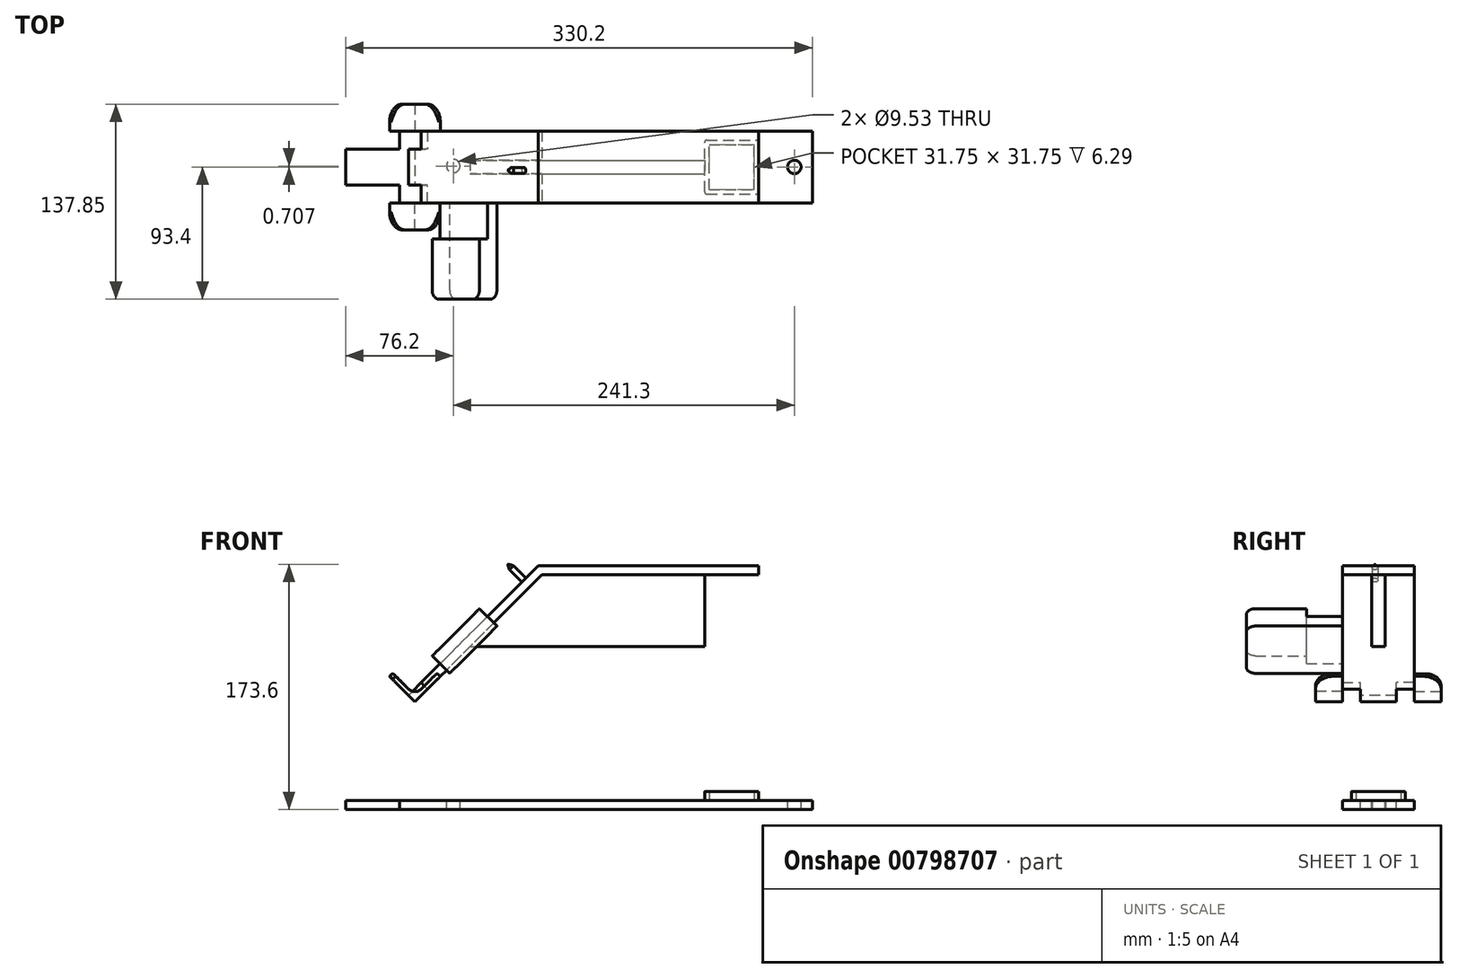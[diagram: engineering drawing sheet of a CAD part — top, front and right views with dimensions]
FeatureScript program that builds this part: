
annotation { "Feature Type Name" : "Feature", "Feature Type Description" : "" }
export const myFeature = defineFeature(function(context is Context, id is Id, definition is map)
    precondition{}
    {
        {
            assignVariable(context, id + "F0", {"name" : "haut", "anyValue" : 8 - 0.49 - 1 - .25 + 0.03});
        }
        {
            var Q0;
            Q0=qCreatedBy(makeId("Top.planeOp"),FACE);
            var sketch = newSketch(context, id + "F1", { "sketchPlane" : qUnion([Q0])});
            skLineSegment(sketch, "E0.bottom", {"start": v(0, 0) * mm, "end": v(114.3, 0) * mm});
            skLineSegment(sketch, "E0.top", {"start": v(0, 50.8) * mm, "end": v(114.3, 50.8) * mm});
            skLineSegment(sketch, "E0.left", {"start": v(0, 0) * mm, "end": v(0, 50.8) * mm});
            skLineSegment(sketch, "E0.right", {"start": v(114.3, 0) * mm, "end": v(114.3, 50.8) * mm});
            skLineSegment(sketch, "E1.bottom", {"start": v(0, 0) * mm, "end": v(-177.8, 0) * mm});
            skLineSegment(sketch, "E1.top", {"start": v(0, 50.8) * mm, "end": v(-177.8, 50.8) * mm});
            skLineSegment(sketch, "E1.right", {"start": v(-215.9, 12.7) * mm, "end": v(-215.9, 38.1) * mm});
            skLineSegment(sketch, "E2.top", {"start": v(-215.9, 38.1) * mm, "end": v(-177.8, 38.1) * mm});
            skLineSegment(sketch, "E2.right", {"start": v(-177.8, 50.8) * mm, "end": v(-177.8, 38.1) * mm});
            skLineSegment(sketch, "E3.top", {"start": v(-215.9, 12.7) * mm, "end": v(-177.8, 12.7) * mm});
            skLineSegment(sketch, "E3.right", {"start": v(-177.8, 0) * mm, "end": v(-177.8, 12.7) * mm});
            skCircle(sketch, "E4", {"center": v(101.6, 25.4) * mm, "radius": 4.76 * mm});
            skCircle(sketch, "E5", {"center": v(-139.7, 26.1) * mm, "radius": 4.76 * mm});
            skSolve(sketch);
        }
        {
            var Q0;
            Q0=qSketchRegion(id+"F1",true);
            extrude(context, id + "F2", {"entities" : qUnion([Q0]), "oppositeDirection" : true, "depth" : 6.35 * mm, "offsetDistance" : 25.4 * mm});
        }
        {
            var Q0;
            Q0=makeQuery(id+"F2.opExtrude","CAP_FACE",FACE,{"disambiguationData":[OSD([sQuery(id+"F1.wireOp",EDGE,"E0.bottom"),sQuery(id+"F1.wireOp",EDGE,"E0.top"),sQuery(id+"F1.wireOp",EDGE,"E0.left"),sQuery(id+"F1.wireOp",EDGE,"E0.right")])],"isStart":true});
            var sketch = newSketch(context, id + "F3", { "sketchPlane" : qUnion([Q0])});
            skLineSegment(sketch, "E6.bottom", {"start": v(38.1, 6.35) * mm, "end": v(76.2, 6.35) * mm});
            skLineSegment(sketch, "E6.top", {"start": v(38.1, 44.45) * mm, "end": v(76.2, 44.45) * mm});
            skLineSegment(sketch, "E6.left", {"start": v(38.1, 6.35) * mm, "end": v(38.1, 44.45) * mm});
            skLineSegment(sketch, "E6.right", {"start": v(76.2, 6.35) * mm, "end": v(76.2, 44.45) * mm});
            skLineSegment(sketch, "E7.0", {"start": v(41.27, 41.28) * mm, "end": v(73.03, 41.28) * mm});
            skLineSegment(sketch, "E7.1", {"start": v(41.27, 9.52) * mm, "end": v(41.27, 41.28) * mm});
            skLineSegment(sketch, "E7.2", {"start": v(41.27, 9.52) * mm, "end": v(73.03, 9.53) * mm});
            skLineSegment(sketch, "E7.3", {"start": v(73.03, 9.53) * mm, "end": v(73.03, 41.28) * mm});
            skSolve(sketch);
        }
        {
            var Q0;
            Q0=qSketchRegion(id+"F3",true);
            extrude(context, id + "F4", {"entities" : qUnion([Q0]), "operationType" : NewBodyOperationType.ADD, "depth" : (getVariable(context, 'haut')) * mm, "offsetDistance" : 25.4 * mm});
        }
        {
            var Q0;
            Q0=makeQuery(id+"F4.opExtrude","SWEPT_FACE",FACE,{"disambiguationData":[OSD([sQuery(id+"F3.wireOp",EDGE,"E6.bottom")])]});
            var sketch = newSketch(context, id + "F5", { "sketchPlane" : qUnion([Q0])});
            skLineSegment(sketch, "E8", {"start": v(76.2, 159.77) * mm, "end": v(-77.04, 159.77) * mm});
            skLineSegment(sketch, "E9", {"start": v(-77.04, 159.77) * mm, "end": v(-166.85, 69.96) * mm});
            skLineSegment(sketch, "E10.0", {"start": v(76.2, 166.12) * mm, "end": v(-79.67, 166.12) * mm});
            skLineSegment(sketch, "E11.0", {"start": v(-79.67, 166.12) * mm, "end": v(-171.34, 74.45) * mm});
            skLineSegment(sketch, "E12", {"start": v(-166.85, 69.96) * mm, "end": v(-171.34, 74.45) * mm});
            skLineSegment(sketch, "E13", {"start": v(76.2, 159.77) * mm, "end": v(76.2, 166.12) * mm});
            skSolve(sketch);
        }
        {
            var Q0;
            Q0=qSketchRegion(id+"F5",true);
            extrude(context, id + "F6", {"entities" : qUnion([Q0]), "operationType" : NewBodyOperationType.ADD, "oppositeDirection" : true, "depth" : 44.45 * mm, "offsetDistance" : 25.4 * mm, "hasSecondDirection" : true, "secondDirectionOppositeDirection" : false, "secondDirectionDepth" : 6.35 * mm});
        }
        {
            var Q0;
            Q0=makeQuery(id+"F6.opExtrude","SWEPT_FACE",FACE,{"disambiguationData":[OSD([sQuery(id+"F5.wireOp",EDGE,"E11.0")])]});
            var sketch = newSketch(context, id + "F7", { "sketchPlane" : qUnion([Q0])});
            skCircle(sketch, "E14", {"center": v(-23.02, 46.84) * mm, "radius": 2.04 * mm});
            skLineSegment(sketch, "E15.direction1", {"start": v(-23.02, 46.84) * mm, "end": v(2.38, 46.84) * mm, "construction": true});
            skLineSegment(sketch, "E15.direction2", {"start": v(-23.02, 46.84) * mm, "end": v(-23.02, -80.16) * mm, "construction": true});
            skSolve(sketch);
        }
        {
            var Q0;
            Q0=qSketchRegion(id+"F7",true);
            extrude(context, id + "F8", {"entities" : qUnion([Q0]), "operationType" : NewBodyOperationType.ADD, "depth" : 15.88 * mm, "offsetDistance" : 25.4 * mm});
        }
        {
            var Q0;
            Q0=makeQuery(id+"F8.opExtrude","CAP_EDGE",EDGE,{"disambiguationData":[OSD([sQuery(id+"F7.wireOp",EDGE,"E14")])],"isStart":false});
            var Q1;
            Q1=makeQuery(id+"F8.opExtrude","CAP_EDGE",EDGE,{"disambiguationData":[OSD([sQuery(id+"F7.wireOp",EDGE,"E15.0.1.0")])],"isStart":false});
            chamfer(context, id + "F9", {"entities" : qUnion([Q0, Q1]), "chamferType" : ChamferType.OFFSET_ANGLE, "width" : 2.03 * mm, "oppositeDirection" : false, "angle" : 60 * degree, "tangentPropagation" : true});
        }
        {
            var Q0;
            Q0=makeQuery(id+"F7.imprint","IMPRINT",FACE,{"disambiguationData":[TD([[makeQuery(id+"F7.imprint","IMPRINT",EDGE,{"derivedFrom":sQuery(id+"F7.wireOp",EDGE,"E14")}),-1.0]])]});
            var sketch = newSketch(context, id + "F10", { "sketchPlane" : qUnion([Q0])});
            skLineSegment(sketch, "E16.bottom", {"start": v(-50.8, -68.5) * mm, "end": v(-38.1, -68.5) * mm});
            skLineSegment(sketch, "E16.top", {"start": v(-50.8, -55.8) * mm, "end": v(-38.1, -55.8) * mm});
            skLineSegment(sketch, "E16.left", {"start": v(-50.8, -68.5) * mm, "end": v(-50.8, -55.8) * mm});
            skLineSegment(sketch, "E16.right", {"start": v(-38.1, -68.5) * mm, "end": v(-38.1, -55.8) * mm});
            skLineSegment(sketch, "E17.bottom", {"start": v(0, -68.5) * mm, "end": v(-12.7, -68.5) * mm});
            skLineSegment(sketch, "E17.top", {"start": v(0, -55.8) * mm, "end": v(-12.7, -55.8) * mm});
            skLineSegment(sketch, "E17.left", {"start": v(0, -68.5) * mm, "end": v(0, -55.8) * mm});
            skLineSegment(sketch, "E17.right", {"start": v(-12.7, -68.5) * mm, "end": v(-12.7, -55.8) * mm});
            skSolve(sketch);
        }
        {
            var Q0;
            Q0=qSketchRegion(id+"F10",true);
            extrude(context, id + "F11", {"entities" : qUnion([Q0]), "operationType" : NewBodyOperationType.REMOVE, "oppositeDirection" : true, "depth" : 25.4 * mm, "offsetDistance" : 25.4 * mm});
        }
        {
            var Q0;
            Q0=makeQuery(id+"F6.opExtrude","CAP_FACE",FACE,{"disambiguationData":[OSD([sQuery(id+"F5.wireOp",EDGE,"E8"),sQuery(id+"F5.wireOp",EDGE,"E9"),sQuery(id+"F5.wireOp",EDGE,"E10.0"),sQuery(id+"F5.wireOp",EDGE,"E11.0"),sQuery(id+"F5.wireOp",EDGE,"E12"),sQuery(id+"F5.wireOp",EDGE,"E13")])],"isStart":false});
            var sketch = newSketch(context, id + "F12", { "sketchPlane" : qUnion([Q0])});
            skLineSegment(sketch, "E18", {"start": v(148.89, 87.92) * mm, "end": v(166.85, 69.96) * mm});
            skLineSegment(sketch, "E19", {"start": v(148.89, 87.92) * mm, "end": v(151.13, 90.17) * mm});
            skLineSegment(sketch, "E20", {"start": v(166.85, 69.96) * mm, "end": v(184.8, 87.92) * mm});
            skLineSegment(sketch, "E21.0", {"start": v(151.13, 90.17) * mm, "end": v(166.85, 74.45) * mm});
            skLineSegment(sketch, "E22.0", {"start": v(166.85, 74.45) * mm, "end": v(182.56, 90.17) * mm});
            skLineSegment(sketch, "E23.0", {"start": v(182.56, 90.17) * mm, "end": v(184.8, 87.92) * mm});
            skSolve(sketch);
        }
        {
            var Q0;
            Q0=qSketchRegion(id+"F12",true);
            extrude(context, id + "F13", {"entities" : qUnion([Q0]), "depth" : 19.05 * mm, "offsetDistance" : 25.4 * mm});
        }
        {
            var Q0;
            Q0=makeQuery(id+"F13.opExtrude","CAP_EDGE",EDGE,{"disambiguationData":[OSD([sQuery(id+"F12.wireOp",EDGE,"E23.0")])],"isStart":false});
            fillet(context, id + "F14", {"entities" : qUnion([Q0]), "radius" : 12.7 * mm, "tangentPropagation" : true, "allowEdgeOverflow" : false});
        }
        {
            var Q0;
            Q0=makeQuery(id+"F13.opExtrude","CAP_EDGE",EDGE,{"disambiguationData":[OSD([sQuery(id+"F12.wireOp",EDGE,"E19")])],"isStart":false});
            fillet(context, id + "F15", {"entities" : qUnion([Q0]), "radius" : 12.7 * mm, "tangentPropagation" : true, "allowEdgeOverflow" : false});
        }
        {
            var Q0;
            Q0=makeQuery(id+"F13.opExtrude","SWEPT_EDGE",EDGE,{"disambiguationData":[OSD([sQuery(id+"F12.wireOp",EDGE,"E21.0"),sQuery(id+"F12.wireOp",EDGE,"E22.0")])]});
            fillet(context, id + "F16", {"entities" : qUnion([Q0]), "radius" : 6.35 * mm, "tangentPropagation" : true, "allowEdgeOverflow" : false});
        }
        {
            var Q0;
            Q0=makeQuery(id+"F13.opExtrude","SWEPT_EDGE",EDGE,{"disambiguationData":[OSD([sQuery(id+"F12.wireOp",EDGE,"E22.0"),sQuery(id+"F12.wireOp",EDGE,"E23.0")])]});
            var Q1;
            Q1=makeQuery(id+"F13.opExtrude","SWEPT_EDGE",EDGE,{"disambiguationData":[OSD([sQuery(id+"F12.wireOp",EDGE,"E19"),sQuery(id+"F12.wireOp",EDGE,"E21.0")])]});
            fillet(context, id + "F17", {"entities" : qUnion([Q0, Q1]), "radius" : 1.59 * mm, "allowEdgeOverflow" : false});
        }
        {
            var Q0;
            Q0=makeQuery(id+"F13.opExtrude","SWEPT_BODY",BODY,{"disambiguationData":[OSD([sQuery(id+"F12.wireOp",EDGE,"E18"),sQuery(id+"F12.wireOp",EDGE,"E19"),sQuery(id+"F12.wireOp",EDGE,"E20"),sQuery(id+"F12.wireOp",EDGE,"E21.0"),sQuery(id+"F12.wireOp",EDGE,"E22.0"),sQuery(id+"F12.wireOp",EDGE,"E23.0")])]});
            var Q1;
            {var subQ0=sQuery(id+"F5.wireOp",EDGE,"E9");Q1=makeQuery(id+"F5.imprint","IMPRINT",FACE,{"disambiguationData":[TD([[makeQuery(id+"F5.imprint","IMPRINT",EDGE,{"derivedFrom":subQ0}),-1.0]])]});}
            mirror(context, id + "F18", {"entities" : qUnion([Q0]), "mirrorPlane" : qUnion([Q1])});
        }
        {
            var Q0;
            Q0=makeQuery(id+"F18.opPattern","COPY",BODY,{"derivedFrom":makeQuery(id+"F13.opExtrude","SWEPT_BODY",BODY,{"disambiguationData":[OSD([sQuery(id+"F12.wireOp",EDGE,"E18"),sQuery(id+"F12.wireOp",EDGE,"E19"),sQuery(id+"F12.wireOp",EDGE,"E20"),sQuery(id+"F12.wireOp",EDGE,"E21.0"),sQuery(id+"F12.wireOp",EDGE,"E22.0"),sQuery(id+"F12.wireOp",EDGE,"E23.0")])]}),"instanceName":"1"});
            var Q1;
            Q1=makeQuery(id+"F18.opPattern","COPY",EDGE,{"derivedFrom":makeQuery(id+"F13.opExtrude","SWEPT_EDGE",EDGE,{"disambiguationData":[OSD([sQuery(id+"F12.wireOp",EDGE,"E18"),sQuery(id+"F12.wireOp",EDGE,"E20")])]}),"instanceName":"1"});
            var Q2;
            Q2=makeQuery(id+"F18.opPattern","COPY",EDGE,{"derivedFrom":makeQuery(id+"F13.opExtrude","SWEPT_EDGE",EDGE,{"disambiguationData":[OSD([sQuery(id+"F12.wireOp",EDGE,"E18"),sQuery(id+"F12.wireOp",EDGE,"E20")])]}),"instanceName":"1"});
            transform(context, id + "F19", {"entities" : qUnion([Q0]), "transformType" : TransformType.TRANSLATION_DISTANCE, "transformDirection" : qUnion([Q2]), "distance" : 38.1 * mm, "makeCopy" : false});
        }
        {
            var Q0;
            Q0=makeQuery(id+"F7.imprint","IMPRINT",FACE,{"disambiguationData":[TD([[makeQuery(id+"F7.imprint","IMPRINT",EDGE,{"derivedFrom":sQuery(id+"F7.wireOp",EDGE,"E14")}),-1.0]])]});
            var sketch = newSketch(context, id + "F20", { "sketchPlane" : qUnion([Q0])});
            skLineSegment(sketch, "E24.bottom", {"start": v(68, -36.92) * mm, "end": v(0, -36.92) * mm});
            skLineSegment(sketch, "E24.top", {"start": v(68, 10.32) * mm, "end": v(0, 10.32) * mm});
            skLineSegment(sketch, "E24.left", {"start": v(68, -36.92) * mm, "end": v(68, 10.32) * mm});
            skLineSegment(sketch, "E24.right", {"start": v(0, -36.92) * mm, "end": v(0, 10.32) * mm});
            skSolve(sketch);
        }
        {
            var Q0;
            Q0=qSketchRegion(id+"F20",true);
            extrude(context, id + "F21", {"entities" : qUnion([Q0]), "oppositeDirection" : true, "depth" : 9.52 * mm, "offsetDistance" : 25.4 * mm, "hasSecondDirection" : true, "secondDirectionOppositeDirection" : false, "secondDirectionDepth" : 7.94 * mm});
        }
        {
            var Q0;
            Q0=makeQuery(id+"F21.opExtrude","CAP_FACE",FACE,{"disambiguationData":[OSD([sQuery(id+"F20.wireOp",EDGE,"E24.bottom"),sQuery(id+"F20.wireOp",EDGE,"E24.top"),sQuery(id+"F20.wireOp",EDGE,"E24.left"),sQuery(id+"F20.wireOp",EDGE,"E24.right")])],"isStart":true});
            var sketch = newSketch(context, id + "F22", { "sketchPlane" : qUnion([Q0])});
            skLineSegment(sketch, "E25.bottom", {"start": v(0, -36.92) * mm, "end": v(25.4, -36.92) * mm});
            skLineSegment(sketch, "E25.top", {"start": v(0, 10.32) * mm, "end": v(25.4, 10.32) * mm});
            skLineSegment(sketch, "E25.left", {"start": v(0, -36.92) * mm, "end": v(0, 10.32) * mm});
            skLineSegment(sketch, "E25.right", {"start": v(25.4, -36.92) * mm, "end": v(25.4, 10.32) * mm});
            skSolve(sketch);
        }
        {
            var Q0;
            Q0=qSketchRegion(id+"F22",true);
            extrude(context, id + "F23", {"entities" : qUnion([Q0]), "operationType" : NewBodyOperationType.REMOVE, "oppositeDirection" : true, "depth" : 7.94 * mm, "offsetDistance" : 25.4 * mm});
        }
        {
            var Q0;
            Q0=makeQuery(id+"F4.opExtrude","SWEPT_FACE",FACE,{"disambiguationData":[OSD([sQuery(id+"F3.wireOp",EDGE,"E6.left")])]});
            var sketch = newSketch(context, id + "F24", { "sketchPlane" : qUnion([Q0])});
            skLineSegment(sketch, "E26.0", {"start": v(-30.16, 159.77) * mm, "end": v(-30.16, 108.97) * mm});
            skLineSegment(sketch, "E26.1", {"start": v(-30.16, 159.77) * mm, "end": v(-20.64, 159.77) * mm});
            skLineSegment(sketch, "E26.2", {"start": v(-20.64, 159.77) * mm, "end": v(-20.64, 108.97) * mm});
            skLineSegment(sketch, "E26.3", {"start": v(-30.16, 108.97) * mm, "end": v(-20.64, 108.97) * mm});
            skSolve(sketch);
        }
        {
            var Q0;
            Q0=qSketchRegion(id+"F24",true);
            var Q1;
            Q1=makeQuery(id+"F6.opExtrude","SWEPT_FACE",FACE,{"disambiguationData":[OSD([sQuery(id+"F5.wireOp",EDGE,"E9")])]});
            extrude(context, id + "F25", {"entities" : qUnion([Q0]), "operationType" : NewBodyOperationType.ADD, "endBound" : BoundingType.UP_TO_SURFACE, "depth" : 115.14 * mm, "endBoundEntityFace" : qUnion([Q1]), "offsetDistance" : 25.4 * mm});
        }
        {
            var Q0;
            Q0=makeQuery(id+"F21.opExtrude","SWEPT_EDGE",EDGE,{"disambiguationData":[OSD([sQuery(id+"F20.wireOp",EDGE,"E24.top"),sQuery(id+"F20.wireOp",EDGE,"E24.left")])]});
            var Q1;
            Q1=makeQuery(id+"F21.opExtrude","SWEPT_EDGE",EDGE,{"disambiguationData":[OSD([sQuery(id+"F20.wireOp",EDGE,"E24.bottom"),sQuery(id+"F20.wireOp",EDGE,"E24.left")])]});
            fillet(context, id + "F26", {"entities" : qUnion([Q0, Q1]), "radius" : 6.35 * mm, "tangentPropagation" : true, "allowEdgeOverflow" : false});
        }
        {
            var Q0;
            Q0=makeQuery(id+"F4.opExtrude","SWEPT_EDGE",EDGE,{"disambiguationData":[OSD([sQuery(id+"F3.wireOp",EDGE,"E6.bottom"),sQuery(id+"F3.wireOp",EDGE,"E6.right")])]});
            var Q1;
            Q1=makeQuery(id+"F4.opExtrude","SWEPT_EDGE",EDGE,{"disambiguationData":[OSD([sQuery(id+"F3.wireOp",EDGE,"E6.bottom"),sQuery(id+"F3.wireOp",EDGE,"E6.left")])]});
            var Q2;
            Q2=makeQuery(id+"F4.opExtrude","SWEPT_EDGE",EDGE,{"disambiguationData":[OSD([sQuery(id+"F3.wireOp",EDGE,"E6.top"),sQuery(id+"F3.wireOp",EDGE,"E6.right")])]});
            var Q3;
            Q3=makeQuery(id+"F4.opExtrude","SWEPT_EDGE",EDGE,{"disambiguationData":[OSD([sQuery(id+"F3.wireOp",EDGE,"E6.top"),sQuery(id+"F3.wireOp",EDGE,"E6.left")])]});
            fillet(context, id + "F27", {"entities" : qUnion([Q0, Q1, Q2, Q3]), "radius" : 1.59 * mm, "tangentPropagation" : true, "allowEdgeOverflow" : false});
        }
    });
